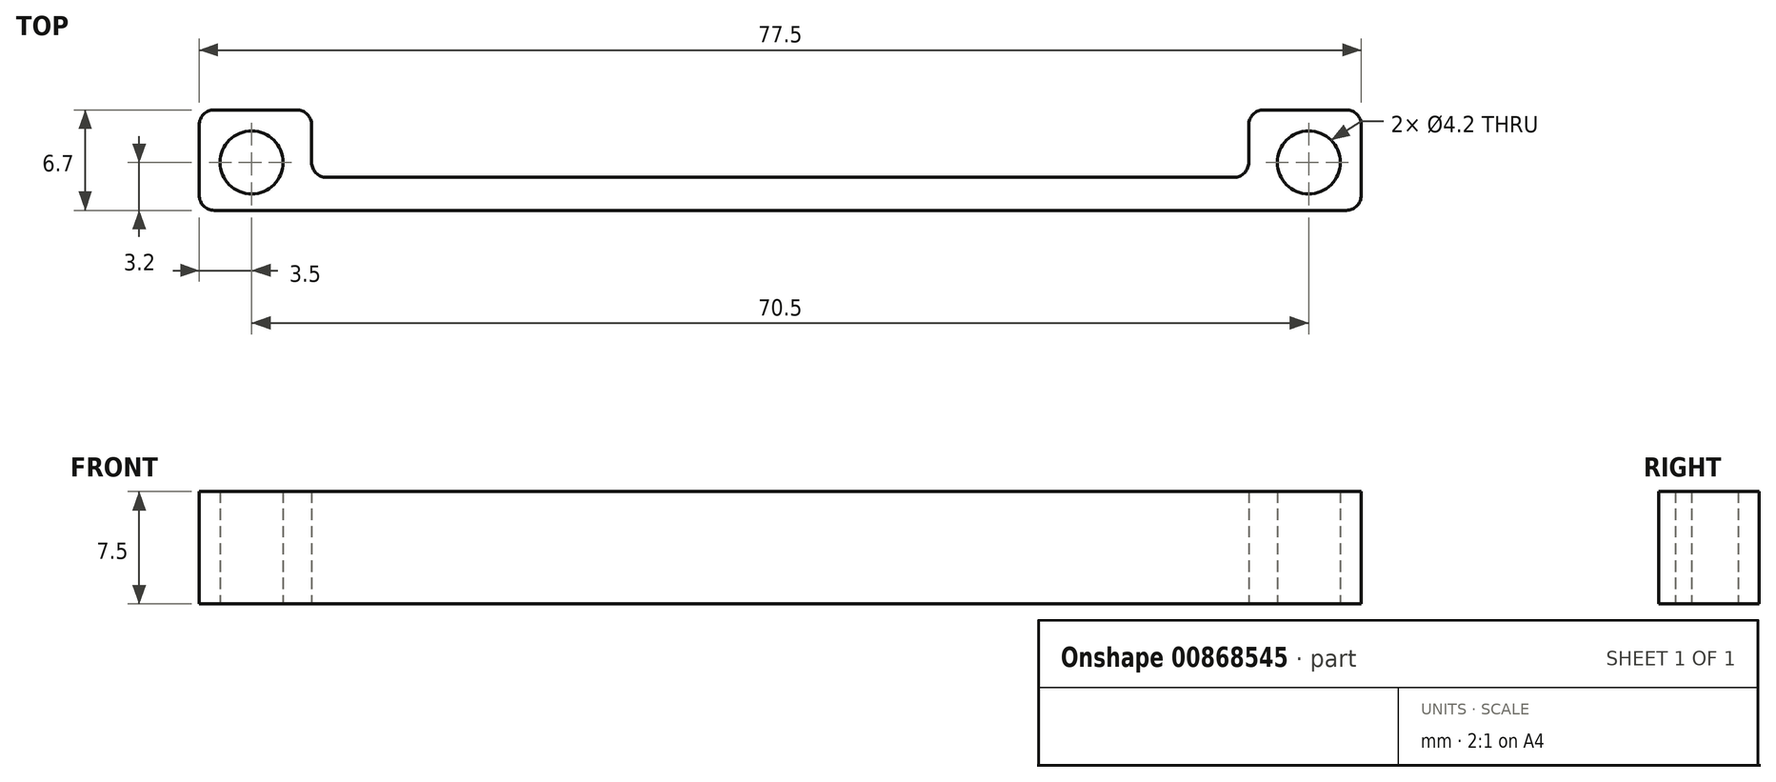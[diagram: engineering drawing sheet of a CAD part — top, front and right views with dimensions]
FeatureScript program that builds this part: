
annotation { "Feature Type Name" : "Feature", "Feature Type Description" : "" }
export const myFeature = defineFeature(function(context is Context, id is Id, definition is map)
    precondition{}
    {
        {
            var Q0;
            Q0=qCreatedBy(makeId("Top.planeOp"),FACE);
            var sketch = newSketch(context, id + "F0", { "sketchPlane" : qUnion([Q0])});
            skLineSegment(sketch, "E0.bottom", {"start": v(-38.75, 23.5) * mm, "end": v(38.75, 23.5) * mm, "construction": true});
            skLineSegment(sketch, "E0.top", {"start": v(-38.75, -23.5) * mm, "end": v(38.75, -23.5) * mm, "construction": true});
            skLineSegment(sketch, "E0.left", {"start": v(-38.75, 23.5) * mm, "end": v(-38.75, -23.5) * mm, "construction": true});
            skLineSegment(sketch, "E0.right", {"start": v(38.75, 23.5) * mm, "end": v(38.75, -23.5) * mm, "construction": true});
            skCircle(sketch, "E1", {"center": v(-35.25, 20) * mm, "radius": 2.1 * mm});
            skLineSegment(sketch, "E2", {"start": v(0, 23.5) * mm, "end": v(0, -23.5) * mm, "construction": true});
            skLineSegment(sketch, "E3.bottom", {"start": v(-30.75, 23.5) * mm, "end": v(9.25, 23.5) * mm, "construction": true});
            skLineSegment(sketch, "E3.top", {"start": v(-30.75, 19.5) * mm, "end": v(9.25, 19.5) * mm, "construction": true});
            skLineSegment(sketch, "E3.left", {"start": v(-30.75, 23.5) * mm, "end": v(-30.75, 19.5) * mm, "construction": true});
            skLineSegment(sketch, "E3.right", {"start": v(9.25, 23.5) * mm, "end": v(9.25, 19.5) * mm, "construction": true});
            skLineSegment(sketch, "E4", {"start": v(-38.75, 16.5) * mm, "end": v(38.75, 16.5) * mm, "construction": true});
            skLineSegment(sketch, "E5.bottom", {"start": v(-37.75, 23.5) * mm, "end": v(-32.25, 23.5) * mm});
            skLineSegment(sketch, "E5.left", {"start": v(-38.75, 22.5) * mm, "end": v(-38.75, 17.8) * mm});
            skLineSegment(sketch, "E6.bottom", {"start": v(-30.25, 19) * mm, "end": v(0, 19) * mm});
            skLineSegment(sketch, "E7", {"start": v(-37.75, 16.8) * mm, "end": v(0, 16.8) * mm});
            skLineSegment(sketch, "E8", {"start": v(-31.25, 20) * mm, "end": v(-31.25, 22.5) * mm});
            skPoint(sketch, "E9.visualSharp", {"position": v(-31.25, 19) * mm});
            skArc(sketch, "E9.filletArc", {"start": v(-31.25, 20) * mm, "mid": v(-30.96, 19.3) * mm, "end": v(-30.25, 19) * mm});
            skPoint(sketch, "E10.visualSharp", {"position": v(-31.25, 23.5) * mm});
            skArc(sketch, "E10.filletArc", {"start": v(-31.25, 22.5) * mm, "mid": v(-31.54, 23.2) * mm, "end": v(-32.25, 23.5) * mm});
            skPoint(sketch, "E11.visualSharp", {"position": v(-38.75, 23.5) * mm});
            skArc(sketch, "E11.filletArc", {"start": v(-37.75, 23.5) * mm, "mid": v(-38.46, 23.2) * mm, "end": v(-38.75, 22.5) * mm});
            skPoint(sketch, "E12.visualSharp", {"position": v(-38.75, 16.8) * mm});
            skArc(sketch, "E12.filletArc", {"start": v(-38.75, 17.8) * mm, "mid": v(-38.46, 17.1) * mm, "end": v(-37.75, 16.8) * mm});
            skCircle(sketch, "E13.MirrorC", {"center": v(35.25, 20) * mm, "radius": 2.1 * mm});
            skLineSegment(sketch, "E14.MirrorCS", {"start": v(30.25, 19) * mm, "end": v(0, 19) * mm});
            skArc(sketch, "E15.MirrorCS", {"start": v(31.25, 20) * mm, "mid": v(30.96, 19.3) * mm, "end": v(30.25, 19) * mm});
            skLineSegment(sketch, "E16.MirrorCS", {"start": v(31.25, 20) * mm, "end": v(31.25, 22.5) * mm});
            skArc(sketch, "E17.MirrorCS", {"start": v(31.25, 22.5) * mm, "mid": v(31.54, 23.2) * mm, "end": v(32.25, 23.5) * mm});
            skLineSegment(sketch, "E18.MirrorCS", {"start": v(37.75, 16.8) * mm, "end": v(0, 16.8) * mm});
            skArc(sketch, "E19.MirrorCS", {"start": v(38.75, 17.8) * mm, "mid": v(38.46, 17.1) * mm, "end": v(37.75, 16.8) * mm});
            skLineSegment(sketch, "E20.MirrorCS", {"start": v(37.75, 23.5) * mm, "end": v(32.25, 23.5) * mm});
            skLineSegment(sketch, "E21.MirrorCS", {"start": v(38.75, 22.5) * mm, "end": v(38.75, 17.8) * mm});
            skArc(sketch, "E22.MirrorCS", {"start": v(37.75, 23.5) * mm, "mid": v(38.46, 23.2) * mm, "end": v(38.75, 22.5) * mm});
            skSolve(sketch);
        }
        {
            var Q0;
            Q0 = qSketchRegion(id + "F0", true);
            extrude(context, id + "F1", {"entities" : qUnion([Q0]), "depth" : 7.5 * mm, "offsetDistance" : 25 * mm});
        }
    });
